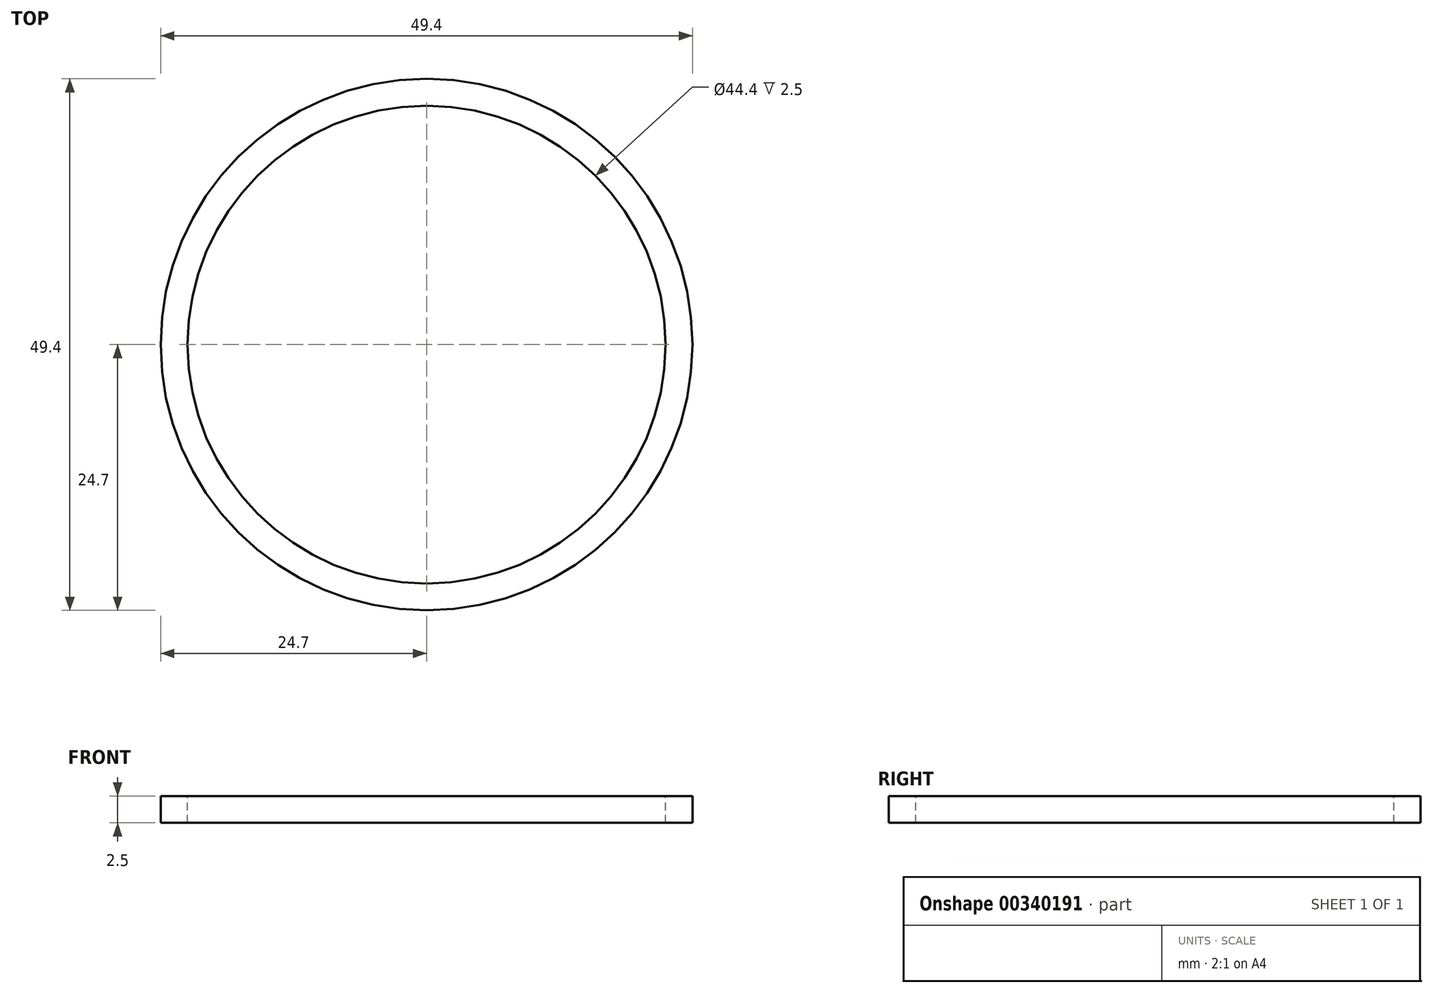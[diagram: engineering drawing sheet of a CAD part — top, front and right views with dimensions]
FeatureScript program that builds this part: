
annotation { "Feature Type Name" : "Feature", "Feature Type Description" : "" }
export const myFeature = defineFeature(function(context is Context, id is Id, definition is map)
    precondition{}
    {
        {
            var Q0;
            Q0=qCreatedBy(makeId("Front.planeOp"),FACE);
            var sketch = newSketch(context, id + "F0", { "sketchPlane" : qUnion([Q0])});
            skLineSegment(sketch, "E0.bottom", {"start": v(1.25, 1.25) * mm, "end": v(-1.25, 1.25) * mm});
            skLineSegment(sketch, "E0.top", {"start": v(1.25, -1.25) * mm, "end": v(-1.25, -1.25) * mm});
            skLineSegment(sketch, "E0.left", {"start": v(1.25, 1.25) * mm, "end": v(1.25, -1.25) * mm});
            skLineSegment(sketch, "E0.right", {"start": v(-1.25, 1.25) * mm, "end": v(-1.25, -1.25) * mm});
            skPoint(sketch, "E0.middle", {"position": v(0, 0) * mm});
            skSolve(sketch);
        }
        {
            var Q0;
            Q0=qCreatedBy(makeId("Top.planeOp"),FACE);
            var sketch = newSketch(context, id + "F1", { "sketchPlane" : qUnion([Q0])});
            skLineSegment(sketch, "E1", {"start": v(0, 0) * mm, "end": v(0, -50.45) * mm, "construction": true});
            skArc(sketch, "E2", {"start": v(0, 0) * mm, "mid": v(23.45, 23.45) * mm, "end": v(46.9, 0) * mm});
            skLineSegment(sketch, "E3", {"start": v(0, 0) * mm, "end": v(12.9, 0) * mm, "construction": true});
            skArc(sketch, "E4.MirrorCS", {"start": v(0, 0) * mm, "mid": v(23.45, -23.45) * mm, "end": v(46.9, 0) * mm});
            skSolve(sketch);
        }
        {
            var Q0;
            Q0=makeQuery(id+"F0.imprint","IMPRINT",FACE,{"disambiguationData":[TD([[makeQuery(id+"F0.imprint","IMPRINT",EDGE,{"derivedFrom":sQuery(id+"F0.wireOp",EDGE,"E0.bottom")}),1.0]])]});
            var Q1;
            Q1=sQuery(id+"F1.wireOp",EDGE,"E2");
            var Q2;
            Q2=sQuery(id+"F1.wireOp",EDGE,"E4.MirrorCS");
            sweep(context, id + "F2", {"profiles" : qUnion([Q0]), "path" : qUnion([Q1, Q2])});
        }
    });
